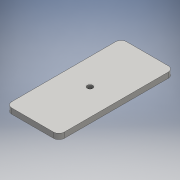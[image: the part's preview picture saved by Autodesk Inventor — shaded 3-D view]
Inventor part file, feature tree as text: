
AUTODESK INVENTOR PART (.ipt)
format: ipt  version: 2016 (Build 200138000, 138)  size: 99,840 bytes
history: native  units: mm
features: sketch x2, extrude x1, hole x1
ambient origin geometry x8: Origin, YZ Plane, XZ Plane, XY Plane, X Axis, Y Axis, Z Axis, Center Point
bodies: Solid1 (feature_tree)
feature tree (4):
  extrude  "Extrusion1"  [1 undecoded]
  hole  "Hole1"  [1 undecoded]
  sketch  "Sketch1"  dims[d0=6.0mm d1=0.0mm]
  sketch  "Sketch2"  dims[d2=3.7mm d3=6.0mm d4=6.0mm d5=3.5mm d6=90.0deg d7=8.0mm d8=20.594885mm]
note: 2 required parameter values undecoded (feature->parameter linkage not recoverable at this tier; creation-order binding heuristic only, values carry confidence <= 0.55)
